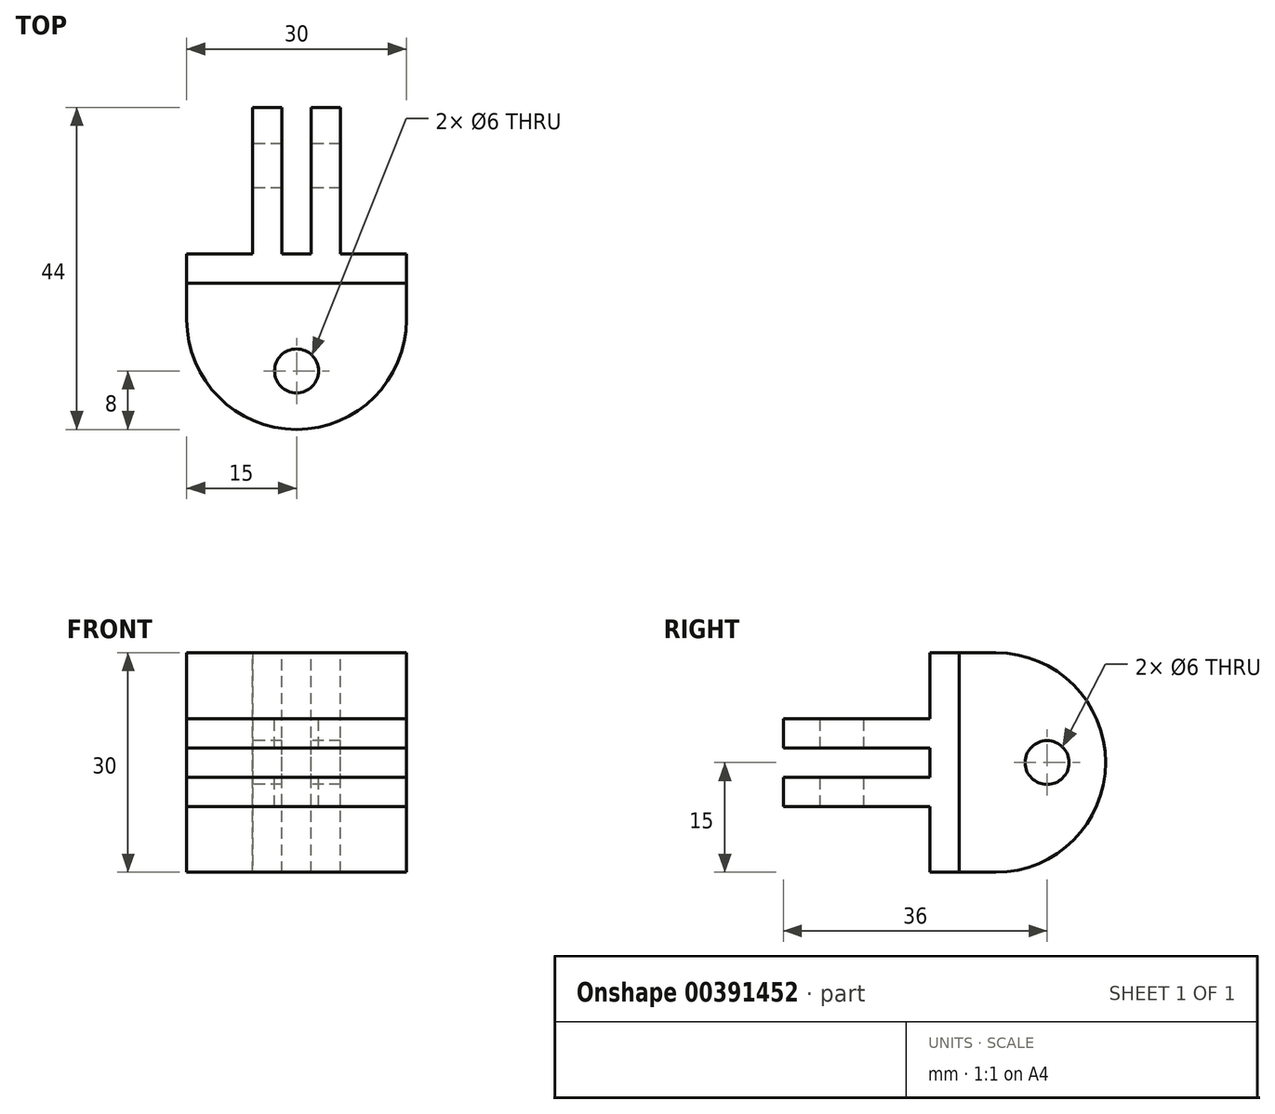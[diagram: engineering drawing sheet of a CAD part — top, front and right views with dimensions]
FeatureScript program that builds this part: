
annotation { "Feature Type Name" : "Feature", "Feature Type Description" : "" }
export const myFeature = defineFeature(function(context is Context, id is Id, definition is map)
    precondition{}
    {
        {
            var Q0;
            Q0=qCreatedBy(makeId("Front.planeOp"),FACE);
            var sketch = newSketch(context, id + "F0", { "sketchPlane" : qUnion([Q0])});
            skLineSegment(sketch, "E0.bottom", {"start": v(15, 15) * mm, "end": v(-15, 15) * mm});
            skLineSegment(sketch, "E0.top", {"start": v(15, -15) * mm, "end": v(-15, -15) * mm});
            skLineSegment(sketch, "E0.left", {"start": v(15, 15) * mm, "end": v(15, -15) * mm});
            skLineSegment(sketch, "E0.right", {"start": v(-15, 15) * mm, "end": v(-15, -15) * mm});
            skPoint(sketch, "E0.middle", {"position": v(0, 0) * mm});
            skSolve(sketch);
        }
        {
            var Q0;
            Q0=makeQuery(id+"F0.imprint","IMPRINT",FACE,{"disambiguationData":[TD([[makeQuery(id+"F0.imprint","IMPRINT",EDGE,{"derivedFrom":sQuery(id+"F0.wireOp",EDGE,"E0.bottom")}),1.0]])]});
            extrude(context, id + "F1", {"entities" : qUnion([Q0]), "depth" : 4 * mm});
        }
        {
            var Q0;
            Q0=makeQuery(id+"F1.opExtrude","CAP_FACE",FACE,{"disambiguationData":[OSD([sQuery(id+"F0.wireOp",EDGE,"E0.bottom"),sQuery(id+"F0.wireOp",EDGE,"E0.top"),sQuery(id+"F0.wireOp",EDGE,"E0.left"),sQuery(id+"F0.wireOp",EDGE,"E0.right")])],"isStart":true});
            var sketch = newSketch(context, id + "F2", { "sketchPlane" : qUnion([Q0])});
            skLineSegment(sketch, "E1.bottom", {"start": v(6, -15) * mm, "end": v(2, -15) * mm});
            skLineSegment(sketch, "E1.top", {"start": v(6, 15) * mm, "end": v(2, 15) * mm});
            skLineSegment(sketch, "E1.left", {"start": v(6, -15) * mm, "end": v(6, 15) * mm});
            skLineSegment(sketch, "E1.right", {"start": v(2, -15) * mm, "end": v(2, 15) * mm});
            skLineSegment(sketch, "E2.bottom", {"start": v(-6, -15) * mm, "end": v(-2, -15) * mm});
            skLineSegment(sketch, "E2.top", {"start": v(-6, 15) * mm, "end": v(-2, 15) * mm});
            skLineSegment(sketch, "E2.left", {"start": v(-6, -15) * mm, "end": v(-6, 15) * mm});
            skLineSegment(sketch, "E2.right", {"start": v(-2, -15) * mm, "end": v(-2, 15) * mm});
            skLineSegment(sketch, "E3", {"start": v(0, -15) * mm, "end": v(0, 15) * mm, "construction": true});
            skSolve(sketch);
        }
        {
            var Q0;
            Q0 = qSketchRegion(id + "F2", true);
            extrude(context, id + "F3", {"entities" : qUnion([Q0]), "operationType" : NewBodyOperationType.ADD, "depth" : 20 * mm});
        }
        {
            var Q0;
            Q0=makeQuery(id+"F3.opExtrude","SWEPT_FACE",FACE,{"disambiguationData":[OSD([sQuery(id+"F2.wireOp",EDGE,"E1.left")])]});
            var sketch = newSketch(context, id + "F4", { "sketchPlane" : qUnion([Q0])});
            skLineSegment(sketch, "E4", {"start": v(-20, 15) * mm, "end": v(-5, 15) * mm});
            skLineSegment(sketch, "E5", {"start": v(-20, -15) * mm, "end": v(-5, -15) * mm});
            skArc(sketch, "E6", {"start": v(-20, 0) * mm, "mid": v(-15.6, -10.6) * mm, "end": v(-5, -15) * mm});
            skArc(sketch, "E7", {"start": v(-5, 15) * mm, "mid": v(-15.6, 10.6) * mm, "end": v(-20, 0) * mm});
            skSolve(sketch);
        }
        {
            var Q0;
            {var subQ0=sQuery(id+"F4.wireOp",EDGE,"E5");Q0=makeQuery(id+"F4.imprint","IMPRINT",FACE,{"disambiguationData":[TD([[makeQuery(id+"F4.imprint","IMPRINT",EDGE,{"derivedFrom":subQ0}),1.0]])]});}
            var Q1;
            {var subQ0=sQuery(id+"F4.wireOp",EDGE,"E4");Q1=makeQuery(id+"F4.imprint","IMPRINT",FACE,{"disambiguationData":[TD([[makeQuery(id+"F4.imprint","IMPRINT",EDGE,{"derivedFrom":subQ0}),-1.0]])]});}
            extrude(context, id + "F5", {"entities" : qUnion([Q0, Q1]), "operationType" : NewBodyOperationType.REMOVE, "oppositeDirection" : true, "depth" : 25 * mm});
        }
        {
            var Q0;
            Q0=makeQuery(id+"F3.opExtrude","SWEPT_FACE",FACE,{"disambiguationData":[OSD([sQuery(id+"F2.wireOp",EDGE,"E1.left")])]});
            var sketch = newSketch(context, id + "F6", { "sketchPlane" : qUnion([Q0])});
            skCircle(sketch, "E8", {"center": v(-12, 0) * mm, "radius": 3 * mm});
            skSolve(sketch);
        }
        {
            var Q0;
            Q0 = qSketchRegion(id + "F6", true);
            extrude(context, id + "F7", {"entities" : qUnion([Q0]), "operationType" : NewBodyOperationType.REMOVE, "oppositeDirection" : true, "depth" : 25 * mm});
        }
        {
            var Q0;
            Q0=makeQuery(id+"F1.opExtrude","CAP_FACE",FACE,{"disambiguationData":[OSD([sQuery(id+"F0.wireOp",EDGE,"E0.bottom"),sQuery(id+"F0.wireOp",EDGE,"E0.top"),sQuery(id+"F0.wireOp",EDGE,"E0.left"),sQuery(id+"F0.wireOp",EDGE,"E0.right")])],"isStart":false});
            var sketch = newSketch(context, id + "F8", { "sketchPlane" : qUnion([Q0])});
            skLineSegment(sketch, "E9.bottom", {"start": v(-15, 2) * mm, "end": v(15, 2) * mm});
            skLineSegment(sketch, "E9.top", {"start": v(-15, 6) * mm, "end": v(15, 6) * mm});
            skLineSegment(sketch, "E9.left", {"start": v(-15, 2) * mm, "end": v(-15, 6) * mm});
            skLineSegment(sketch, "E9.right", {"start": v(15, 2) * mm, "end": v(15, 6) * mm});
            skLineSegment(sketch, "E10.bottom", {"start": v(-15, -2) * mm, "end": v(15, -2) * mm});
            skLineSegment(sketch, "E10.top", {"start": v(-15, -6) * mm, "end": v(15, -6) * mm});
            skLineSegment(sketch, "E10.left", {"start": v(-15, -2) * mm, "end": v(-15, -6) * mm});
            skLineSegment(sketch, "E10.right", {"start": v(15, -2) * mm, "end": v(15, -6) * mm});
            skSolve(sketch);
        }
        {
            var Q0;
            Q0 = qSketchRegion(id + "F8", true);
            extrude(context, id + "F9", {"entities" : qUnion([Q0]), "operationType" : NewBodyOperationType.ADD, "depth" : 20 * mm});
        }
        {
            var Q0;
            Q0=makeQuery(id+"F9.opExtrude","SWEPT_FACE",FACE,{"disambiguationData":[OSD([sQuery(id+"F8.wireOp",EDGE,"E9.top")])]});
            var sketch = newSketch(context, id + "F10", { "sketchPlane" : qUnion([Q0])});
            skArc(sketch, "E11", {"start": v(0, -24) * mm, "mid": v(10.6, -19.6) * mm, "end": v(15, -9) * mm});
            skArc(sketch, "E12", {"start": v(-15, -9) * mm, "mid": v(-10.6, -19.6) * mm, "end": v(0, -24) * mm});
            skLineSegment(sketch, "E13", {"start": v(15, -24) * mm, "end": v(15, -9) * mm});
            skLineSegment(sketch, "E14", {"start": v(15, -24) * mm, "end": v(0, -24) * mm});
            skLineSegment(sketch, "E15", {"start": v(-15, -9) * mm, "end": v(-15, -24) * mm});
            skLineSegment(sketch, "E16", {"start": v(-15, -24) * mm, "end": v(0, -24) * mm});
            skSolve(sketch);
        }
        {
            var Q0;
            Q0=makeQuery(id+"F10.imprint","IMPRINT",FACE,{"disambiguationData":[TD([[makeQuery(id+"F10.imprint","IMPRINT",EDGE,{"derivedFrom":sQuery(id+"F10.wireOp",EDGE,"E12")}),-1.0]])]});
            var Q1;
            Q1=makeQuery(id+"F10.imprint","IMPRINT",FACE,{"disambiguationData":[TD([[makeQuery(id+"F10.imprint","IMPRINT",EDGE,{"derivedFrom":sQuery(id+"F10.wireOp",EDGE,"E11")}),-1.0]])]});
            extrude(context, id + "F11", {"entities" : qUnion([Q0, Q1]), "operationType" : NewBodyOperationType.REMOVE, "oppositeDirection" : true, "depth" : 25 * mm});
        }
        {
            var Q0;
            Q0=makeQuery(id+"F9.opExtrude","SWEPT_FACE",FACE,{"disambiguationData":[OSD([sQuery(id+"F8.wireOp",EDGE,"E9.top")])]});
            var sketch = newSketch(context, id + "F12", { "sketchPlane" : qUnion([Q0])});
            skCircle(sketch, "E17", {"center": v(0, -16) * mm, "radius": 3 * mm});
            skSolve(sketch);
        }
        {
            var Q0;
            Q0 = qSketchRegion(id + "F12", true);
            extrude(context, id + "F13", {"entities" : qUnion([Q0]), "operationType" : NewBodyOperationType.REMOVE, "oppositeDirection" : true, "depth" : 25 * mm});
        }
    });
